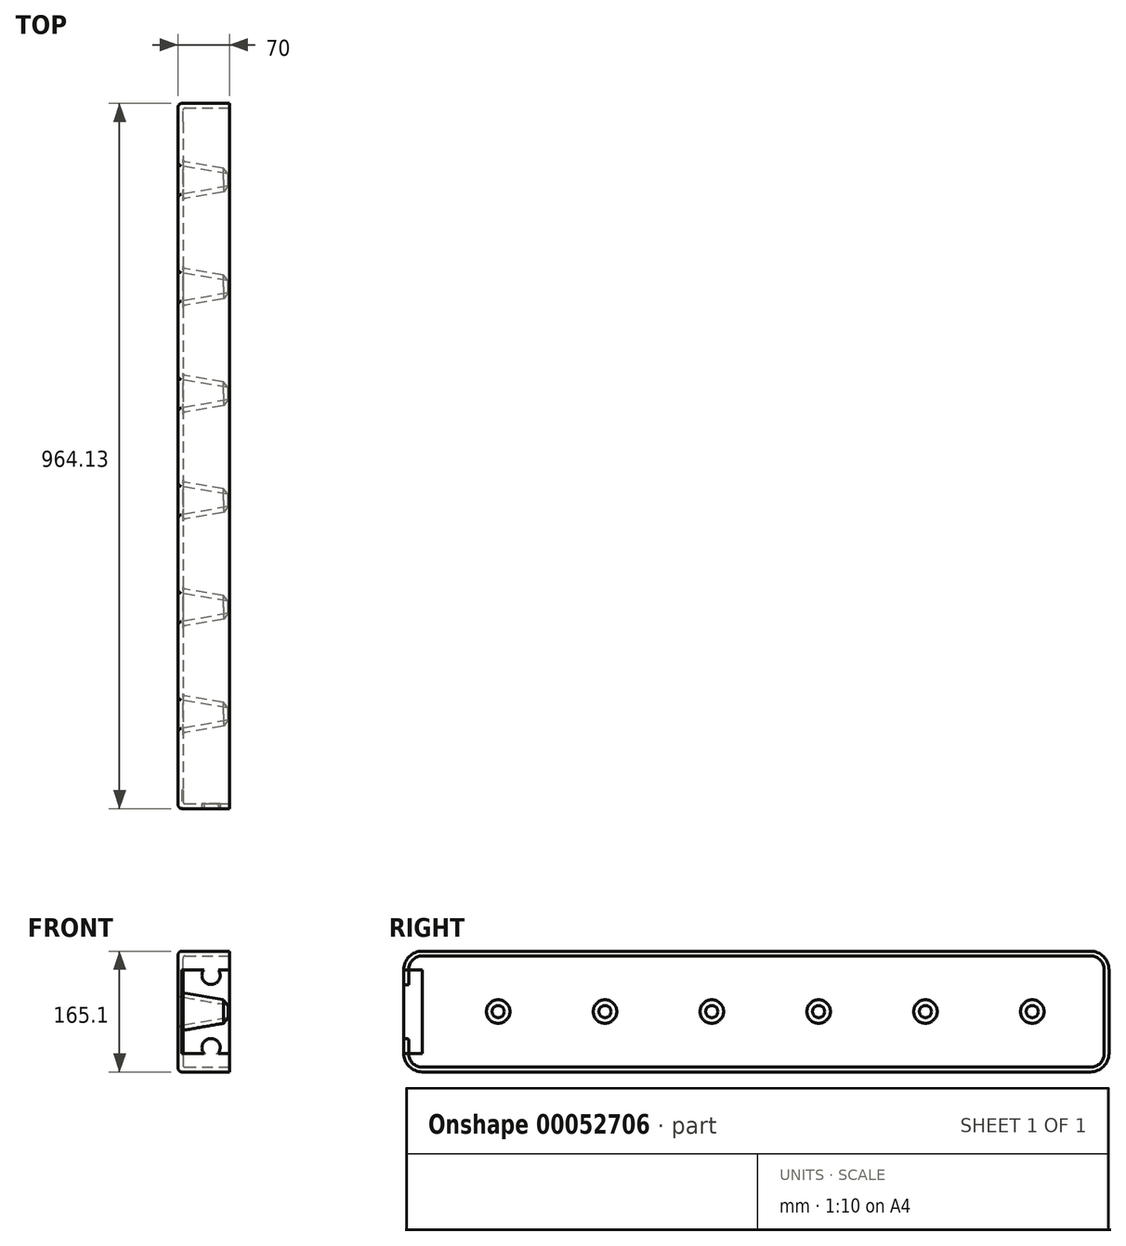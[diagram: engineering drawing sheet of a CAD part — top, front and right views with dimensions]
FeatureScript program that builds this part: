
annotation { "Feature Type Name" : "Feature", "Feature Type Description" : "" }
export const myFeature = defineFeature(function(context is Context, id is Id, definition is map)
    precondition{}
    {
        {
            var Q0;
            Q0=qCreatedBy(makeId("Right.planeOp"),FACE);
            var sketch = newSketch(context, id + "F0", { "sketchPlane" : qUnion([Q0])});
            skLineSegment(sketch, "E0.rect.bottom", {"start": v(-457.5, 82.55) * mm, "end": v(457.5, 82.55) * mm});
            skLineSegment(sketch, "E0.rect.top", {"start": v(-457.5, -82.55) * mm, "end": v(457.5, -82.55) * mm});
            skLineSegment(sketch, "E0.rect.left", {"start": v(-457.5, 82.55) * mm, "end": v(-457.5, -82.55) * mm});
            skLineSegment(sketch, "E0.rect.right", {"start": v(457.5, 82.55) * mm, "end": v(457.5, -82.55) * mm});
            skPoint(sketch, "E0.rect.middle", {"position": v(0, 0) * mm});
            skLineSegment(sketch, "E1.0", {"start": v(-447.34, 72.39) * mm, "end": v(447.34, 72.39) * mm, "construction": true});
            skLineSegment(sketch, "E1.1", {"start": v(-447.34, 72.39) * mm, "end": v(-447.34, -72.39) * mm, "construction": true});
            skLineSegment(sketch, "E1.2", {"start": v(-447.34, -72.39) * mm, "end": v(447.34, -72.39) * mm, "construction": true});
            skLineSegment(sketch, "E1.3", {"start": v(447.34, 72.39) * mm, "end": v(447.34, -72.39) * mm, "construction": true});
            skLineSegment(sketch, "E2", {"start": v(-457.5, 82.55) * mm, "end": v(457.5, -82.55) * mm, "construction": true});
            skLineSegment(sketch, "E3", {"start": v(457.5, 82.55) * mm, "end": v(-457.5, -82.55) * mm, "construction": true});
            skSolve(sketch);
        }
        {
            var Q0;
            Q0=makeQuery(id+"F0.imprint","IMPRINT",FACE,{"disambiguationData":[TD([[makeQuery(id+"F0.imprint","IMPRINT",EDGE,{"derivedFrom":sQuery(id+"F0.wireOp",EDGE,"E0.rect.bottom")}),-1.0]])]});
            extrude(context, id + "F1", {"entities" : qUnion([Q0]), "depth" : 70 * mm});
        }
        {
            var Q0;
            Q0=makeQuery(id+"F1.opExtrude","SWEPT_FACE",FACE,{"disambiguationData":[OSD([sQuery(id+"F0.wireOp",EDGE,"E0.rect.left")])]});
            extrude(context, id + "F2", {"entities" : qUnion([Q0]), "operationType" : NewBodyOperationType.ADD, "depth" : 36.63 * mm});
        }
        {
            var Q0;
            Q0=makeQuery(id+"F1.opExtrude","SWEPT_FACE",FACE,{"disambiguationData":[OSD([sQuery(id+"F0.wireOp",EDGE,"E0.rect.right")])]});
            extrude(context, id + "F3", {"entities" : qUnion([Q0]), "operationType" : NewBodyOperationType.ADD, "depth" : 12.5 * mm});
        }
        {
            var Q0;
            Q0=makeQuery(id+"F0.imprint","IMPRINT",FACE,{"disambiguationData":[TD([[makeQuery(id+"F0.imprint","IMPRINT",EDGE,{"derivedFrom":sQuery(id+"F0.wireOp",EDGE,"E0.rect.bottom")}),-1.0]])]});
            var sketch = newSketch(context, id + "F4", { "sketchPlane" : qUnion([Q0])});
            skLineSegment(sketch, "E4", {"start": v(-457.5, 0) * mm, "end": v(457.5, 0) * mm, "construction": true});
            skCircle(sketch, "E5", {"center": v(-365.13, 0) * mm, "radius": 20.32 * mm});
            skCircle(sketch, "E6", {"center": v(-73.03, 0) * mm, "radius": 20.32 * mm});
            skCircle(sketch, "E7.MirrorC", {"center": v(73.03, 0) * mm, "radius": 20.32 * mm});
            skCircle(sketch, "E8", {"center": v(-219.08, 0) * mm, "radius": 20.32 * mm});
            skCircle(sketch, "E9", {"center": v(219.08, 0) * mm, "radius": 20.32 * mm});
            skCircle(sketch, "E10", {"center": v(365.13, 0) * mm, "radius": 20.32 * mm});
            skSolve(sketch);
        }
        {
            var Q0;
            Q0=qSketchRegion(id+"F4",true);
            extrude(context, id + "F5", {"entities" : qUnion([Q0]), "operationType" : NewBodyOperationType.REMOVE, "endBound" : BoundingType.THROUGH_ALL, "depth" : 25 * mm, "hasDraft" : true, "draftAngle" : 10 * degree, "draftPullDirection" : true});
        }
        {
            var Q0;
            {var subQ0=makeQuery(id+"FMJtkyeOeprAO9Q_1.hole-4.opRevolve","SWEPT_FACE",FACE,{"disambiguationData":[OSD([sQuery(id+"FMJtkyeOeprAO9Q_1.hole-4.sketch.wireOp",EDGE,"cbore_start_line_2")])]});var subQ1=makeQuery(id+"FMJtkyeOeprAO9Q_1.hole-2.boolean.opBoolean","COPY",FACE,{"derivedFrom":makeQuery(id+"FMJtkyeOeprAO9Q_1.hole-2.opRevolve","SWEPT_FACE",FACE,{"disambiguationData":[OSD([sQuery(id+"FMJtkyeOeprAO9Q_1.hole-2.sketch.wireOp",EDGE,"cbore_start_line_2")])]})});var subQ2=sQuery(id+"F0.wireOp",EDGE,"E0.rect.top");var subQ3=makeQuery(id+"F1.opExtrude","SWEPT_FACE",FACE,{"disambiguationData":[OSD([subQ2])]});var subQ4=makeQuery(id+"FMJtkyeOeprAO9Q_1.hole-3.opRevolve","SWEPT_FACE",FACE,{"disambiguationData":[OSD([sQuery(id+"FMJtkyeOeprAO9Q_1.hole-3.sketch.wireOp",EDGE,"cbore_start_line_2")])]});var subQ5=makeQuery(id+"FMJtkyeOeprAO9Q_1.hole-3.boolean.opBoolean","COPY",FACE,{"disambiguationData":[OD(1.0)],"derivedFrom":subQ4});var subQ6=makeQuery(id+"FMJtkyeOeprAO9Q_1.hole-0.opRevolve","SWEPT_FACE",FACE,{"disambiguationData":[OSD([sQuery(id+"FMJtkyeOeprAO9Q_1.hole-0.sketch.wireOp",EDGE,"cbore_start_line_2")])]});var subQ7=makeQuery(id+"FMJtkyeOeprAO9Q_1.hole-0.boolean.opBoolean","COPY",FACE,{"disambiguationData":[OD(1.0)],"derivedFrom":subQ6});var subQ8=makeQuery(id+"FMJtkyeOeprAO9Q_1.hole-1.boolean.opBoolean","COPY",FACE,{"derivedFrom":makeQuery(id+"FMJtkyeOeprAO9Q_1.hole-1.opRevolve","SWEPT_FACE",FACE,{"disambiguationData":[OSD([sQuery(id+"FMJtkyeOeprAO9Q_1.hole-1.sketch.wireOp",EDGE,"cbore_start_line_2")])]})});var subQ9=sQuery(id+"F0.wireOp",EDGE,"E0.rect.bottom");var subQ10=makeQuery(id+"F1.opExtrude","SWEPT_FACE",FACE,{"disambiguationData":[OSD([subQ9])]});var subQ11=sQuery(id+"F0.wireOp",EDGE,"E0.rect.left");var subQ12=makeQuery(id+"F1.opExtrude","SWEPT_FACE",FACE,{"disambiguationData":[OSD([subQ11])]});var subQ13=sQuery(id+"F0.wireOp",EDGE,"E0.rect.right");var subQ14=makeQuery(id+"F1.opExtrude","SWEPT_FACE",FACE,{"disambiguationData":[OSD([subQ13])]});Q0=makeQuery(id+"FMJtkyeOeprAO9Q_1.hole-7.boolean.opBoolean","SPLIT",FACE,{"disambiguationData":[TD([subQ10,subQ3,subQ12,subQ14,subQ7,subQ8,subQ1,subQ5,makeQuery(id+"FMJtkyeOeprAO9Q_1.hole-4.boolean.opBoolean","COPY",FACE,{"disambiguationData":[OD(1.0)],"derivedFrom":subQ0}),makeQuery(id+"FMJtkyeOeprAO9Q_1.hole-5.boolean.opBoolean","COPY",FACE,{"derivedFrom":makeQuery(id+"FMJtkyeOeprAO9Q_1.hole-5.opRevolve","SWEPT_FACE",FACE,{"disambiguationData":[OSD([sQuery(id+"FMJtkyeOeprAO9Q_1.hole-5.sketch.wireOp",EDGE,"cbore_start_line_2")])]})}),makeQuery(id+"FMJtkyeOeprAO9Q_1.hole-6.boolean.opBoolean","COPY",FACE,{"derivedFrom":makeQuery(id+"FMJtkyeOeprAO9Q_1.hole-6.opRevolve","SWEPT_FACE",FACE,{"disambiguationData":[OSD([sQuery(id+"FMJtkyeOeprAO9Q_1.hole-6.sketch.wireOp",EDGE,"cbore_start_line_2")])]})}),makeQuery(id+"FMJtkyeOeprAO9Q_1.hole-7.opRevolve","SWEPT_FACE",FACE,{"disambiguationData":[OSD([sQuery(id+"FMJtkyeOeprAO9Q_1.hole-7.sketch.wireOp",EDGE,"cbore_start_line_2")])]})])],"derivedFrom":makeQuery(id+"FMJtkyeOeprAO9Q_1.hole-4.boolean.opBoolean","SPLIT",FACE,{"disambiguationData":[TD([subQ10,subQ3,subQ12,subQ14,subQ7,subQ8,subQ1,subQ5,subQ0])],"derivedFrom":makeQuery(id+"FMJtkyeOeprAO9Q_1.hole-3.boolean.opBoolean","SPLIT",FACE,{"disambiguationData":[TD([subQ10,subQ3,subQ12,subQ14,subQ7,subQ8,subQ1,subQ4])],"derivedFrom":makeQuery(id+"FMJtkyeOeprAO9Q_1.hole-0.boolean.opBoolean","SPLIT",FACE,{"disambiguationData":[TD([subQ10,subQ3,subQ12,subQ14,subQ6])],"derivedFrom":makeQuery(id+"F1.opExtrude","CAP_FACE",FACE,{"disambiguationData":[OSD([subQ9,subQ2,subQ11,subQ13])],"isStart":true})})})})});}
            fillet(context, id + "F6", {"entities" : qUnion([Q0]), "radius" : 5 * mm, "tangentPropagation" : true, "allowEdgeOverflow" : false});
        }
        {
            var Q0;
            Q0=makeQuery(id+"F2.opExtrude","CAP_EDGE",EDGE,{"disambiguationData":[OSD([sQuery(id+"F0.wireOp",EDGE,"E0.rect.bottom"),sQuery(id+"F0.wireOp",EDGE,"E0.rect.left")])],"isStart":false});
            var Q1;
            Q1=makeQuery(id+"F2.opExtrude","CAP_EDGE",EDGE,{"disambiguationData":[OSD([sQuery(id+"F0.wireOp",EDGE,"E0.rect.top"),sQuery(id+"F0.wireOp",EDGE,"E0.rect.left")])],"isStart":false});
            var Q2;
            Q2=makeQuery(id+"F3.opExtrude","CAP_EDGE",EDGE,{"disambiguationData":[OSD([sQuery(id+"F0.wireOp",EDGE,"E0.rect.top"),sQuery(id+"F0.wireOp",EDGE,"E0.rect.right")])],"isStart":false});
            var Q3;
            Q3=makeQuery(id+"F3.opExtrude","CAP_EDGE",EDGE,{"disambiguationData":[OSD([sQuery(id+"F0.wireOp",EDGE,"E0.rect.bottom"),sQuery(id+"F0.wireOp",EDGE,"E0.rect.right")])],"isStart":false});
            fillet(context, id + "F7", {"entities" : qUnion([Q0, Q1, Q2, Q3]), "radius" : 25.4 * mm, "tangentPropagation" : true, "allowEdgeOverflow" : false});
        }
        {
            var Q0;
            Q0=makeQuery(id+"F1.opExtrude","CAP_FACE",FACE,{"disambiguationData":[OSD([sQuery(id+"F0.wireOp",EDGE,"E0.rect.bottom"),sQuery(id+"F0.wireOp",EDGE,"E0.rect.top"),sQuery(id+"F0.wireOp",EDGE,"E0.rect.left"),sQuery(id+"F0.wireOp",EDGE,"E0.rect.right")])],"isStart":false});
            shell(context, id + "F8", {"entities" : qUnion([Q0]), "thickness" : 6.5 * mm});
        }
        {
            var Q0;
            {var subQ0=makeQuery(id+"FMJtkyeOeprAO9Q_1.hole-4.opRevolve","SWEPT_FACE",FACE,{"disambiguationData":[OSD([sQuery(id+"FMJtkyeOeprAO9Q_1.hole-4.sketch.wireOp",EDGE,"cbore_start_line_2")])]});var subQ1=makeQuery(id+"FMJtkyeOeprAO9Q_1.hole-2.boolean.opBoolean","COPY",FACE,{"derivedFrom":makeQuery(id+"FMJtkyeOeprAO9Q_1.hole-2.opRevolve","SWEPT_FACE",FACE,{"disambiguationData":[OSD([sQuery(id+"FMJtkyeOeprAO9Q_1.hole-2.sketch.wireOp",EDGE,"cbore_start_line_2")])]})});var subQ2=sQuery(id+"F0.wireOp",EDGE,"E0.rect.top");var subQ3=makeQuery(id+"F1.opExtrude","SWEPT_FACE",FACE,{"disambiguationData":[OSD([subQ2])]});var subQ4=makeQuery(id+"FMJtkyeOeprAO9Q_1.hole-3.opRevolve","SWEPT_FACE",FACE,{"disambiguationData":[OSD([sQuery(id+"FMJtkyeOeprAO9Q_1.hole-3.sketch.wireOp",EDGE,"cbore_start_line_2")])]});var subQ5=makeQuery(id+"FMJtkyeOeprAO9Q_1.hole-3.boolean.opBoolean","COPY",FACE,{"disambiguationData":[OD(1.0)],"derivedFrom":subQ4});var subQ6=makeQuery(id+"FMJtkyeOeprAO9Q_1.hole-0.opRevolve","SWEPT_FACE",FACE,{"disambiguationData":[OSD([sQuery(id+"FMJtkyeOeprAO9Q_1.hole-0.sketch.wireOp",EDGE,"cbore_start_line_2")])]});var subQ7=makeQuery(id+"FMJtkyeOeprAO9Q_1.hole-0.boolean.opBoolean","COPY",FACE,{"disambiguationData":[OD(1.0)],"derivedFrom":subQ6});var subQ8=makeQuery(id+"FMJtkyeOeprAO9Q_1.hole-1.boolean.opBoolean","COPY",FACE,{"derivedFrom":makeQuery(id+"FMJtkyeOeprAO9Q_1.hole-1.opRevolve","SWEPT_FACE",FACE,{"disambiguationData":[OSD([sQuery(id+"FMJtkyeOeprAO9Q_1.hole-1.sketch.wireOp",EDGE,"cbore_start_line_2")])]})});var subQ9=sQuery(id+"F0.wireOp",EDGE,"E0.rect.bottom");var subQ10=makeQuery(id+"F1.opExtrude","SWEPT_FACE",FACE,{"disambiguationData":[OSD([subQ9])]});var subQ11=sQuery(id+"F0.wireOp",EDGE,"E0.rect.left");var subQ12=makeQuery(id+"F1.opExtrude","SWEPT_FACE",FACE,{"disambiguationData":[OSD([subQ11])]});var subQ13=sQuery(id+"F0.wireOp",EDGE,"E0.rect.right");var subQ14=makeQuery(id+"F1.opExtrude","SWEPT_FACE",FACE,{"disambiguationData":[OSD([subQ13])]});Q0=makeQuery(id+"F8.opShell","OFFSET_FACE",FACE,{"disambiguationData":[OSD([subQ9,subQ2,subQ11,subQ13]),TDD([makeQuery(id+"FMJtkyeOeprAO9Q_1.hole-7.boolean.opBoolean","SPLIT",FACE,{"disambiguationData":[TD([subQ10,subQ3,subQ12,subQ14,subQ7,subQ8,subQ1,subQ5,makeQuery(id+"FMJtkyeOeprAO9Q_1.hole-4.boolean.opBoolean","COPY",FACE,{"disambiguationData":[OD(1.0)],"derivedFrom":subQ0}),makeQuery(id+"FMJtkyeOeprAO9Q_1.hole-5.boolean.opBoolean","COPY",FACE,{"derivedFrom":makeQuery(id+"FMJtkyeOeprAO9Q_1.hole-5.opRevolve","SWEPT_FACE",FACE,{"disambiguationData":[OSD([sQuery(id+"FMJtkyeOeprAO9Q_1.hole-5.sketch.wireOp",EDGE,"cbore_start_line_2")])]})}),makeQuery(id+"FMJtkyeOeprAO9Q_1.hole-6.boolean.opBoolean","COPY",FACE,{"derivedFrom":makeQuery(id+"FMJtkyeOeprAO9Q_1.hole-6.opRevolve","SWEPT_FACE",FACE,{"disambiguationData":[OSD([sQuery(id+"FMJtkyeOeprAO9Q_1.hole-6.sketch.wireOp",EDGE,"cbore_start_line_2")])]})}),makeQuery(id+"FMJtkyeOeprAO9Q_1.hole-7.opRevolve","SWEPT_FACE",FACE,{"disambiguationData":[OSD([sQuery(id+"FMJtkyeOeprAO9Q_1.hole-7.sketch.wireOp",EDGE,"cbore_start_line_2")])]})])],"derivedFrom":makeQuery(id+"FMJtkyeOeprAO9Q_1.hole-4.boolean.opBoolean","SPLIT",FACE,{"disambiguationData":[TD([subQ10,subQ3,subQ12,subQ14,subQ7,subQ8,subQ1,subQ5,subQ0])],"derivedFrom":makeQuery(id+"FMJtkyeOeprAO9Q_1.hole-3.boolean.opBoolean","SPLIT",FACE,{"disambiguationData":[TD([subQ10,subQ3,subQ12,subQ14,subQ7,subQ8,subQ1,subQ4])],"derivedFrom":makeQuery(id+"FMJtkyeOeprAO9Q_1.hole-0.boolean.opBoolean","SPLIT",FACE,{"disambiguationData":[TD([subQ10,subQ3,subQ12,subQ14,subQ6])],"derivedFrom":makeQuery(id+"F1.opExtrude","CAP_FACE",FACE,{"disambiguationData":[OSD([subQ9,subQ2,subQ11,subQ13])],"isStart":true})})})})})])]});}
            fillet(context, id + "F9", {"entities" : qUnion([Q0]), "radius" : 3.17 * mm, "tangentPropagation" : true, "allowEdgeOverflow" : false});
        }
        {
            var Q0;
            {var subQ0=sQuery(id+"F4.wireOp",EDGE,"E5");var subQ1=sQuery(id+"F0.wireOp",EDGE,"E0.rect.right");var subQ2=sQuery(id+"F0.wireOp",EDGE,"E0.rect.left");var subQ3=sQuery(id+"F0.wireOp",EDGE,"E0.rect.top");var subQ4=sQuery(id+"F0.wireOp",EDGE,"E0.rect.bottom");Q0=makeQuery(id+"F8.opShell","OFFSET_EDGE",EDGE,{"disambiguationData":[OSD([subQ4,subQ3,subQ2,subQ1,subQ0]),TDD([makeQuery(id+"F5.boolean.opBoolean","INTERSECT",EDGE,{"derivedFrom":[makeQuery(id+"F3.boolean.opBoolean","MERGE",FACE,{"derivedFrom":[makeQuery(id+"F2.boolean.opBoolean","MERGE",FACE,{"derivedFrom":[makeQuery(id+"F1.opExtrude","CAP_FACE",FACE,{"disambiguationData":[OSD([subQ4,subQ3,subQ2,subQ1])],"isStart":false}),makeQuery(id+"F2.opExtrude","SWEPT_FACE",FACE,{"disambiguationData":[OSD([subQ2]),TDD([makeQuery(id+"F1.opExtrude","CAP_EDGE",EDGE,{"disambiguationData":[OSD([subQ2])],"isStart":false})])]})]}),makeQuery(id+"F3.opExtrude","SWEPT_FACE",FACE,{"disambiguationData":[OSD([subQ1]),TDD([makeQuery(id+"F1.opExtrude","CAP_EDGE",EDGE,{"disambiguationData":[OSD([subQ1])],"isStart":false})])]})]}),makeQuery(id+"F5.opExtrude","SWEPT_FACE",FACE,{"disambiguationData":[OSD([subQ0])]})]})])]});}
            var Q1;
            {var subQ0=sQuery(id+"F4.wireOp",EDGE,"E8");var subQ1=sQuery(id+"F0.wireOp",EDGE,"E0.rect.right");var subQ2=sQuery(id+"F0.wireOp",EDGE,"E0.rect.left");var subQ3=sQuery(id+"F0.wireOp",EDGE,"E0.rect.top");var subQ4=sQuery(id+"F0.wireOp",EDGE,"E0.rect.bottom");Q1=makeQuery(id+"F8.opShell","OFFSET_EDGE",EDGE,{"disambiguationData":[OSD([subQ4,subQ3,subQ2,subQ1,subQ0]),TDD([makeQuery(id+"F5.boolean.opBoolean","INTERSECT",EDGE,{"derivedFrom":[makeQuery(id+"F3.boolean.opBoolean","MERGE",FACE,{"derivedFrom":[makeQuery(id+"F2.boolean.opBoolean","MERGE",FACE,{"derivedFrom":[makeQuery(id+"F1.opExtrude","CAP_FACE",FACE,{"disambiguationData":[OSD([subQ4,subQ3,subQ2,subQ1])],"isStart":false}),makeQuery(id+"F2.opExtrude","SWEPT_FACE",FACE,{"disambiguationData":[OSD([subQ2]),TDD([makeQuery(id+"F1.opExtrude","CAP_EDGE",EDGE,{"disambiguationData":[OSD([subQ2])],"isStart":false})])]})]}),makeQuery(id+"F3.opExtrude","SWEPT_FACE",FACE,{"disambiguationData":[OSD([subQ1]),TDD([makeQuery(id+"F1.opExtrude","CAP_EDGE",EDGE,{"disambiguationData":[OSD([subQ1])],"isStart":false})])]})]}),makeQuery(id+"F5.opExtrude","SWEPT_FACE",FACE,{"disambiguationData":[OSD([subQ0])]})]})])]});}
            var Q2;
            {var subQ0=sQuery(id+"F4.wireOp",EDGE,"E6");var subQ1=sQuery(id+"F0.wireOp",EDGE,"E0.rect.right");var subQ2=sQuery(id+"F0.wireOp",EDGE,"E0.rect.left");var subQ3=sQuery(id+"F0.wireOp",EDGE,"E0.rect.top");var subQ4=sQuery(id+"F0.wireOp",EDGE,"E0.rect.bottom");Q2=makeQuery(id+"F8.opShell","OFFSET_EDGE",EDGE,{"disambiguationData":[OSD([subQ4,subQ3,subQ2,subQ1,subQ0]),TDD([makeQuery(id+"F5.boolean.opBoolean","INTERSECT",EDGE,{"derivedFrom":[makeQuery(id+"F3.boolean.opBoolean","MERGE",FACE,{"derivedFrom":[makeQuery(id+"F2.boolean.opBoolean","MERGE",FACE,{"derivedFrom":[makeQuery(id+"F1.opExtrude","CAP_FACE",FACE,{"disambiguationData":[OSD([subQ4,subQ3,subQ2,subQ1])],"isStart":false}),makeQuery(id+"F2.opExtrude","SWEPT_FACE",FACE,{"disambiguationData":[OSD([subQ2]),TDD([makeQuery(id+"F1.opExtrude","CAP_EDGE",EDGE,{"disambiguationData":[OSD([subQ2])],"isStart":false})])]})]}),makeQuery(id+"F3.opExtrude","SWEPT_FACE",FACE,{"disambiguationData":[OSD([subQ1]),TDD([makeQuery(id+"F1.opExtrude","CAP_EDGE",EDGE,{"disambiguationData":[OSD([subQ1])],"isStart":false})])]})]}),makeQuery(id+"F5.opExtrude","SWEPT_FACE",FACE,{"disambiguationData":[OSD([subQ0])]})]})])]});}
            var Q3;
            {var subQ0=sQuery(id+"F4.wireOp",EDGE,"E7.MirrorC");var subQ1=sQuery(id+"F0.wireOp",EDGE,"E0.rect.right");var subQ2=sQuery(id+"F0.wireOp",EDGE,"E0.rect.left");var subQ3=sQuery(id+"F0.wireOp",EDGE,"E0.rect.top");var subQ4=sQuery(id+"F0.wireOp",EDGE,"E0.rect.bottom");Q3=makeQuery(id+"F8.opShell","OFFSET_EDGE",EDGE,{"disambiguationData":[OSD([subQ4,subQ3,subQ2,subQ1,subQ0]),TDD([makeQuery(id+"F5.boolean.opBoolean","INTERSECT",EDGE,{"derivedFrom":[makeQuery(id+"F3.boolean.opBoolean","MERGE",FACE,{"derivedFrom":[makeQuery(id+"F2.boolean.opBoolean","MERGE",FACE,{"derivedFrom":[makeQuery(id+"F1.opExtrude","CAP_FACE",FACE,{"disambiguationData":[OSD([subQ4,subQ3,subQ2,subQ1])],"isStart":false}),makeQuery(id+"F2.opExtrude","SWEPT_FACE",FACE,{"disambiguationData":[OSD([subQ2]),TDD([makeQuery(id+"F1.opExtrude","CAP_EDGE",EDGE,{"disambiguationData":[OSD([subQ2])],"isStart":false})])]})]}),makeQuery(id+"F3.opExtrude","SWEPT_FACE",FACE,{"disambiguationData":[OSD([subQ1]),TDD([makeQuery(id+"F1.opExtrude","CAP_EDGE",EDGE,{"disambiguationData":[OSD([subQ1])],"isStart":false})])]})]}),makeQuery(id+"F5.opExtrude","SWEPT_FACE",FACE,{"disambiguationData":[OSD([subQ0])]})]})])]});}
            var Q4;
            {var subQ0=sQuery(id+"F4.wireOp",EDGE,"E9");var subQ1=sQuery(id+"F0.wireOp",EDGE,"E0.rect.right");var subQ2=sQuery(id+"F0.wireOp",EDGE,"E0.rect.left");var subQ3=sQuery(id+"F0.wireOp",EDGE,"E0.rect.top");var subQ4=sQuery(id+"F0.wireOp",EDGE,"E0.rect.bottom");Q4=makeQuery(id+"F8.opShell","OFFSET_EDGE",EDGE,{"disambiguationData":[OSD([subQ4,subQ3,subQ2,subQ1,subQ0]),TDD([makeQuery(id+"F5.boolean.opBoolean","INTERSECT",EDGE,{"derivedFrom":[makeQuery(id+"F3.boolean.opBoolean","MERGE",FACE,{"derivedFrom":[makeQuery(id+"F2.boolean.opBoolean","MERGE",FACE,{"derivedFrom":[makeQuery(id+"F1.opExtrude","CAP_FACE",FACE,{"disambiguationData":[OSD([subQ4,subQ3,subQ2,subQ1])],"isStart":false}),makeQuery(id+"F2.opExtrude","SWEPT_FACE",FACE,{"disambiguationData":[OSD([subQ2]),TDD([makeQuery(id+"F1.opExtrude","CAP_EDGE",EDGE,{"disambiguationData":[OSD([subQ2])],"isStart":false})])]})]}),makeQuery(id+"F3.opExtrude","SWEPT_FACE",FACE,{"disambiguationData":[OSD([subQ1]),TDD([makeQuery(id+"F1.opExtrude","CAP_EDGE",EDGE,{"disambiguationData":[OSD([subQ1])],"isStart":false})])]})]}),makeQuery(id+"F5.opExtrude","SWEPT_FACE",FACE,{"disambiguationData":[OSD([subQ0])]})]})])]});}
            var Q5;
            {var subQ0=sQuery(id+"F4.wireOp",EDGE,"E10");var subQ1=sQuery(id+"F0.wireOp",EDGE,"E0.rect.right");var subQ2=sQuery(id+"F0.wireOp",EDGE,"E0.rect.left");var subQ3=sQuery(id+"F0.wireOp",EDGE,"E0.rect.top");var subQ4=sQuery(id+"F0.wireOp",EDGE,"E0.rect.bottom");Q5=makeQuery(id+"F8.opShell","OFFSET_EDGE",EDGE,{"disambiguationData":[OSD([subQ4,subQ3,subQ2,subQ1,subQ0]),TDD([makeQuery(id+"F5.boolean.opBoolean","INTERSECT",EDGE,{"derivedFrom":[makeQuery(id+"F3.boolean.opBoolean","MERGE",FACE,{"derivedFrom":[makeQuery(id+"F2.boolean.opBoolean","MERGE",FACE,{"derivedFrom":[makeQuery(id+"F1.opExtrude","CAP_FACE",FACE,{"disambiguationData":[OSD([subQ4,subQ3,subQ2,subQ1])],"isStart":false}),makeQuery(id+"F2.opExtrude","SWEPT_FACE",FACE,{"disambiguationData":[OSD([subQ2]),TDD([makeQuery(id+"F1.opExtrude","CAP_EDGE",EDGE,{"disambiguationData":[OSD([subQ2])],"isStart":false})])]})]}),makeQuery(id+"F3.opExtrude","SWEPT_FACE",FACE,{"disambiguationData":[OSD([subQ1]),TDD([makeQuery(id+"F1.opExtrude","CAP_EDGE",EDGE,{"disambiguationData":[OSD([subQ1])],"isStart":false})])]})]}),makeQuery(id+"F5.opExtrude","SWEPT_FACE",FACE,{"disambiguationData":[OSD([subQ0])]})]})])]});}
            chamfer(context, id + "F10", {"entities" : qUnion([Q0, Q1, Q2, Q3, Q4, Q5]), "width" : 10 * mm, "tangentPropagation" : true});
        }
        {
            var Q0;
            Q0=makeQuery(id+"F2.opExtrude","CAP_FACE",FACE,{"disambiguationData":[OSD([sQuery(id+"F0.wireOp",EDGE,"E0.rect.left")])],"isStart":false});
            var sketch = newSketch(context, id + "F11", { "sketchPlane" : qUnion([Q0])});
            skCircle(sketch, "E11.0", {"center": v(45, -49.4) * mm, "radius": 12.5 * mm});
            skCircle(sketch, "E12.0", {"center": v(45, 49.4) * mm, "radius": 12.5 * mm});
            skSolve(sketch);
        }
        {
            var Q0;
            {var subQ0=sQuery(id+"F11.wireOp",EDGE,"E11.0");var subQ1=sQuery(id+"F0.wireOp",EDGE,"E0.rect.left");var subQ2=makeQuery(id+"F7.opFillet","BLEND_EDGE",EDGE,{"blendedFrom":[makeQuery(id+"F2.opExtrude","CAP_EDGE",EDGE,{"disambiguationData":[OSD([sQuery(id+"F0.wireOp",EDGE,"E0.rect.top"),subQ1])],"isStart":false}),makeQuery(id+"F2.opExtrude","CAP_FACE",FACE,{"disambiguationData":[OSD([subQ1])],"isStart":false})],"blendedInto":[makeQuery(id+"F2.opExtrude","CAP_FACE",FACE,{"disambiguationData":[OSD([subQ1])],"isStart":false})]});var subQ3=makeQuery(id+"F11.imprint","INTERSECT",VERTEX,{"disambiguationData":[OD(0.0)],"derivedFrom":[subQ2,subQ0]});Q0=makeQuery(id+"F11.imprint","IMPRINT",FACE,{"disambiguationData":[TD([[makeQuery(id+"F11.imprint","IMPRINT",EDGE,{"disambiguationData":[TD([[subQ3,1.0]])],"derivedFrom":subQ0}),-1.0]])]});}
            var Q1;
            {var subQ0=sQuery(id+"F11.wireOp",EDGE,"E11.0");var subQ1=sQuery(id+"F0.wireOp",EDGE,"E0.rect.left");var subQ2=makeQuery(id+"F7.opFillet","BLEND_EDGE",EDGE,{"blendedFrom":[makeQuery(id+"F2.opExtrude","CAP_EDGE",EDGE,{"disambiguationData":[OSD([sQuery(id+"F0.wireOp",EDGE,"E0.rect.top"),subQ1])],"isStart":false}),makeQuery(id+"F2.opExtrude","CAP_FACE",FACE,{"disambiguationData":[OSD([subQ1])],"isStart":false})],"blendedInto":[makeQuery(id+"F2.opExtrude","CAP_FACE",FACE,{"disambiguationData":[OSD([subQ1])],"isStart":false})]});var subQ3=makeQuery(id+"F11.imprint","INTERSECT",VERTEX,{"disambiguationData":[OD(0.0)],"derivedFrom":[subQ2,subQ0]});Q1=makeQuery(id+"F11.imprint","IMPRINT",FACE,{"disambiguationData":[TD([[makeQuery(id+"F11.imprint","IMPRINT",EDGE,{"disambiguationData":[TD([[subQ3,-1.0]])],"derivedFrom":subQ0}),-1.0]])]});}
            var Q2;
            {var subQ0=sQuery(id+"F11.wireOp",EDGE,"E12.0");var subQ1=sQuery(id+"F0.wireOp",EDGE,"E0.rect.left");var subQ2=makeQuery(id+"F7.opFillet","BLEND_EDGE",EDGE,{"blendedFrom":[makeQuery(id+"F2.opExtrude","CAP_EDGE",EDGE,{"disambiguationData":[OSD([sQuery(id+"F0.wireOp",EDGE,"E0.rect.bottom"),subQ1])],"isStart":false}),makeQuery(id+"F2.opExtrude","CAP_FACE",FACE,{"disambiguationData":[OSD([subQ1])],"isStart":false})],"blendedInto":[makeQuery(id+"F2.opExtrude","CAP_FACE",FACE,{"disambiguationData":[OSD([subQ1])],"isStart":false})]});var subQ3=makeQuery(id+"F11.imprint","INTERSECT",VERTEX,{"disambiguationData":[OD(0.0)],"derivedFrom":[subQ2,subQ0]});Q2=makeQuery(id+"F11.imprint","IMPRINT",FACE,{"disambiguationData":[TD([[makeQuery(id+"F11.imprint","IMPRINT",EDGE,{"disambiguationData":[TD([[subQ3,-1.0]])],"derivedFrom":subQ0}),-1.0]])]});}
            var Q3;
            {var subQ0=sQuery(id+"F11.wireOp",EDGE,"E12.0");var subQ1=sQuery(id+"F0.wireOp",EDGE,"E0.rect.left");var subQ2=makeQuery(id+"F7.opFillet","BLEND_EDGE",EDGE,{"blendedFrom":[makeQuery(id+"F2.opExtrude","CAP_EDGE",EDGE,{"disambiguationData":[OSD([sQuery(id+"F0.wireOp",EDGE,"E0.rect.bottom"),subQ1])],"isStart":false}),makeQuery(id+"F2.opExtrude","CAP_FACE",FACE,{"disambiguationData":[OSD([subQ1])],"isStart":false})],"blendedInto":[makeQuery(id+"F2.opExtrude","CAP_FACE",FACE,{"disambiguationData":[OSD([subQ1])],"isStart":false})]});var subQ3=makeQuery(id+"F11.imprint","INTERSECT",VERTEX,{"disambiguationData":[OD(0.0)],"derivedFrom":[subQ2,subQ0]});Q3=makeQuery(id+"F11.imprint","IMPRINT",FACE,{"disambiguationData":[TD([[makeQuery(id+"F11.imprint","IMPRINT",EDGE,{"disambiguationData":[TD([[subQ3,1.0]])],"derivedFrom":subQ0}),-1.0]])]});}
            extrude(context, id + "F12", {"entities" : qUnion([Q0, Q1, Q2, Q3]), "operationType" : NewBodyOperationType.REMOVE, "oppositeDirection" : true, "depth" : 25 * mm});
        }
        {
            var Q0;
            Q0=makeQuery(id+"F12.boolean.opBoolean","INTERSECT",EDGE,{"derivedFrom":[makeQuery(id+"F8.opShell","OFFSET_FACE",FACE,{"disambiguationData":[OSD([sQuery(id+"F0.wireOp",EDGE,"E0.rect.left")])]}),makeQuery(id+"F12.opExtrude","SWEPT_FACE",FACE,{"disambiguationData":[OSD([sQuery(id+"F11.wireOp",EDGE,"E11.0")])]})]});
            var Q1;
            Q1=makeQuery(id+"F12.boolean.opBoolean","COPY",EDGE,{"derivedFrom":makeQuery(id+"F12.opExtrude","CAP_EDGE",EDGE,{"disambiguationData":[OSD([sQuery(id+"F11.wireOp",EDGE,"E12.0")])],"isStart":true})});
            var Q2;
            Q2=makeQuery(id+"F12.boolean.opBoolean","INTERSECT",EDGE,{"derivedFrom":[makeQuery(id+"F7.opFillet","BLEND_FACE",FACE,{"disambiguationData":[OSD([sQuery(id+"F0.wireOp",EDGE,"E0.rect.top"),sQuery(id+"F0.wireOp",EDGE,"E0.rect.left")])]}),makeQuery(id+"F12.opExtrude","SWEPT_FACE",FACE,{"disambiguationData":[OSD([sQuery(id+"F11.wireOp",EDGE,"E11.0")])]})]});
            var Q3;
            Q3=makeQuery(id+"F12.boolean.opBoolean","INTERSECT",EDGE,{"derivedFrom":[makeQuery(id+"F7.opFillet","BLEND_FACE",FACE,{"disambiguationData":[OSD([sQuery(id+"F0.wireOp",EDGE,"E0.rect.bottom"),sQuery(id+"F0.wireOp",EDGE,"E0.rect.left")])]}),makeQuery(id+"F12.opExtrude","SWEPT_FACE",FACE,{"disambiguationData":[OSD([sQuery(id+"F11.wireOp",EDGE,"E12.0")])]})]});
            fillet(context, id + "F13", {"entities" : qUnion([Q0, Q1, Q2, Q3]), "radius" : 2 * mm, "tangentPropagation" : true, "allowEdgeOverflow" : false});
        }
    });
